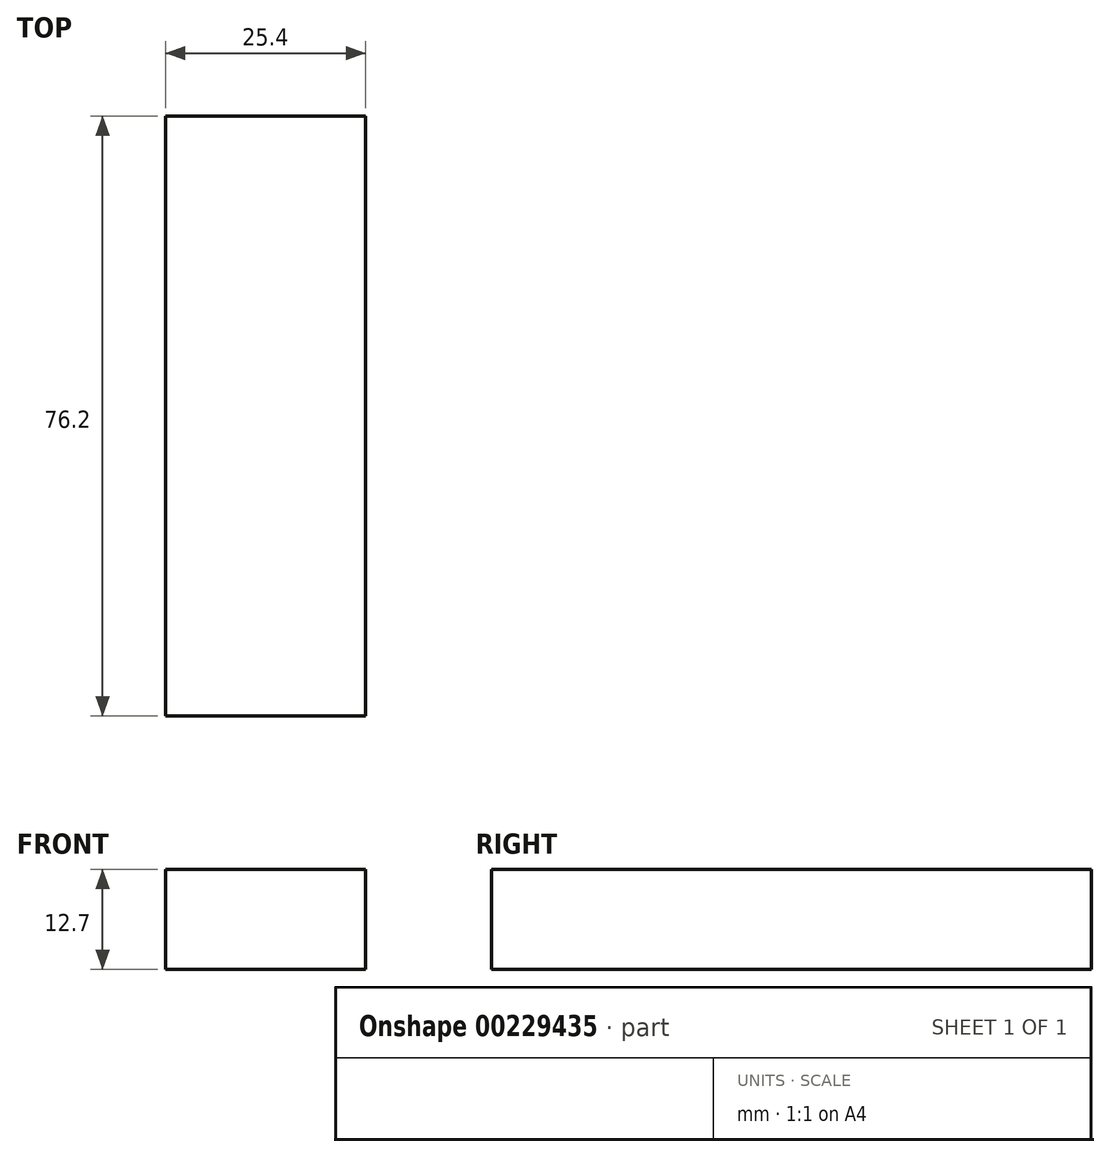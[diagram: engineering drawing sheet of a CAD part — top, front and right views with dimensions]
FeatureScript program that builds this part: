
annotation { "Feature Type Name" : "Feature", "Feature Type Description" : "" }
export const myFeature = defineFeature(function(context is Context, id is Id, definition is map)
    precondition{}
    {
        {
            var Q0;
            Q0=qCreatedBy(makeId("Top.planeOp"),FACE);
            var sketch = newSketch(context, id + "F0", { "sketchPlane" : qUnion([Q0])});
            skLineSegment(sketch, "E0.bottom", {"start": v(0, 0) * mm, "end": v(25.4, 0) * mm});
            skLineSegment(sketch, "E0.top", {"start": v(0, 76.2) * mm, "end": v(25.4, 76.2) * mm});
            skLineSegment(sketch, "E0.left", {"start": v(0, 0) * mm, "end": v(0, 76.2) * mm});
            skLineSegment(sketch, "E0.right", {"start": v(25.4, 0) * mm, "end": v(25.4, 76.2) * mm});
            skSolve(sketch);
        }
        {
            var Q0;
            Q0 = qSketchRegion(id + "F0", true);
            extrude(context, id + "F1", {"entities" : qUnion([Q0]), "oppositeDirection" : true, "depth" : 12.7 * mm});
        }
    });
